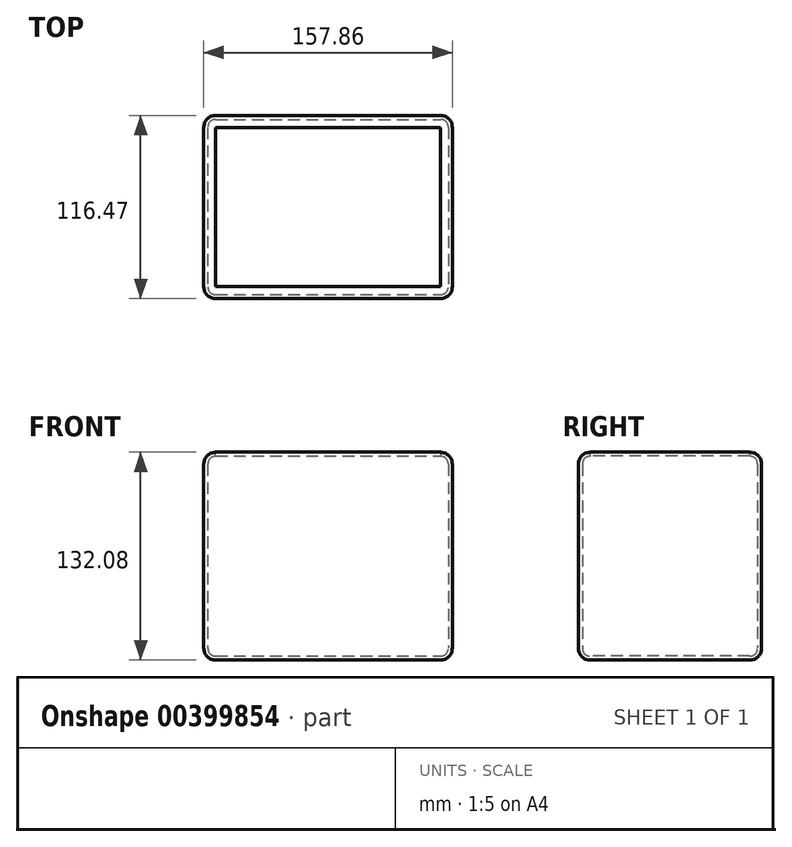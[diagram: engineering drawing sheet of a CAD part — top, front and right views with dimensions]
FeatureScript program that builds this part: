
annotation { "Feature Type Name" : "Feature", "Feature Type Description" : "" }
export const myFeature = defineFeature(function(context is Context, id is Id, definition is map)
    precondition{}
    {
        {
            var Q0;
            Q0=qCreatedBy(makeId("Top.planeOp"),FACE);
            var sketch = newSketch(context, id + "F0", { "sketchPlane" : qUnion([Q0])});
            skLineSegment(sketch, "E0.bottom", {"start": v(-76.56, 55.52) * mm, "end": v(76.22, 55.52) * mm});
            skLineSegment(sketch, "E0.top", {"start": v(-76.56, -55.87) * mm, "end": v(76.22, -55.87) * mm});
            skLineSegment(sketch, "E0.left", {"start": v(-76.56, 55.52) * mm, "end": v(-76.56, -55.87) * mm});
            skLineSegment(sketch, "E0.right", {"start": v(76.22, 55.52) * mm, "end": v(76.22, -55.87) * mm});
            skSolve(sketch);
        }
        {
            var Q0;
            Q0=makeQuery(id+"F0.imprint","IMPRINT",FACE,{"disambiguationData":[TD([[makeQuery(id+"F0.imprint","IMPRINT",EDGE,{"derivedFrom":sQuery(id+"F0.wireOp",EDGE,"E0.bottom")}),-1.0]])]});
            extrude(context, id + "F1", {"entities" : qUnion([Q0]), "depth" : 127 * mm});
        }
        {
            var Q0;
            Q0=makeQuery(id+"F1.opExtrude","CAP_EDGE",EDGE,{"disambiguationData":[OSD([sQuery(id+"F0.wireOp",EDGE,"E0.right")])],"isStart":true});
            fillet(context, id + "F2", {"entities" : qUnion([Q0]), "radius" : 5.08 * mm, "tangentPropagation" : true, "allowEdgeOverflow" : false});
        }
        {
            var Q0;
            Q0=makeQuery(id+"F1.opExtrude","CAP_EDGE",EDGE,{"disambiguationData":[OSD([sQuery(id+"F0.wireOp",EDGE,"E0.left")])],"isStart":true});
            fillet(context, id + "F3", {"entities" : qUnion([Q0]), "radius" : 5.08 * mm, "tangentPropagation" : true, "allowEdgeOverflow" : false});
        }
        {
            var Q0;
            Q0=makeQuery(id+"F1.opExtrude","CAP_EDGE",EDGE,{"disambiguationData":[OSD([sQuery(id+"F0.wireOp",EDGE,"E0.left")])],"isStart":false});
            fillet(context, id + "F4", {"entities" : qUnion([Q0]), "radius" : 5.08 * mm, "tangentPropagation" : true, "allowEdgeOverflow" : false});
        }
        {
            var Q0;
            Q0=makeQuery(id+"F1.opExtrude","CAP_EDGE",EDGE,{"disambiguationData":[OSD([sQuery(id+"F0.wireOp",EDGE,"E0.right")])],"isStart":false});
            fillet(context, id + "F5", {"entities" : qUnion([Q0]), "radius" : 5.08 * mm, "tangentPropagation" : true, "allowEdgeOverflow" : false});
        }
        {
            var Q0;
            Q0=makeQuery(id+"F1.opExtrude","CAP_EDGE",EDGE,{"disambiguationData":[OSD([sQuery(id+"F0.wireOp",EDGE,"E0.bottom")])],"isStart":false});
            fillet(context, id + "F6", {"entities" : qUnion([Q0]), "radius" : 5.08 * mm, "tangentPropagation" : true, "allowEdgeOverflow" : false});
        }
        {
            var Q0;
            Q0=makeQuery(id+"F1.opExtrude","CAP_FACE",FACE,{"disambiguationData":[OSD([sQuery(id+"F0.wireOp",EDGE,"E0.bottom"),sQuery(id+"F0.wireOp",EDGE,"E0.top"),sQuery(id+"F0.wireOp",EDGE,"E0.left"),sQuery(id+"F0.wireOp",EDGE,"E0.right")])],"isStart":false});
            var Q1;
            Q1=makeQuery(id+"F1.opExtrude","SWEPT_FACE",FACE,{"disambiguationData":[OSD([sQuery(id+"F0.wireOp",EDGE,"E0.top")])]});
            fillet(context, id + "F7", {"entities" : qUnion([Q0, Q1]), "radius" : 5.08 * mm, "tangentPropagation" : true, "allowEdgeOverflow" : false});
        }
        {
            var Q0;
            Q0=makeQuery(id+"F1.opExtrude","CAP_FACE",FACE,{"disambiguationData":[OSD([sQuery(id+"F0.wireOp",EDGE,"E0.bottom"),sQuery(id+"F0.wireOp",EDGE,"E0.top"),sQuery(id+"F0.wireOp",EDGE,"E0.left"),sQuery(id+"F0.wireOp",EDGE,"E0.right")])],"isStart":false});
            shell(context, id + "F8", {"entities" : qUnion([Q0]), "thickness" : 2.54 * mm, "oppositeDirection" : true});
        }
    });
